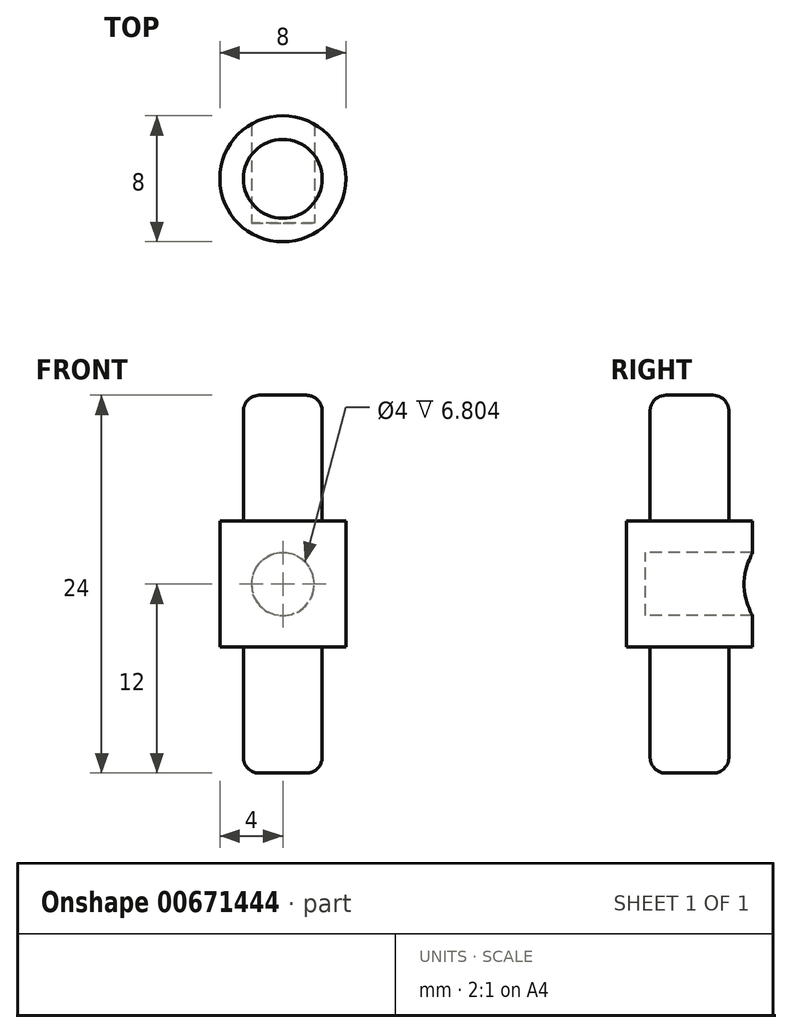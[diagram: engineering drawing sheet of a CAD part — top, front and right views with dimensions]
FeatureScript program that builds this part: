
annotation { "Feature Type Name" : "Feature", "Feature Type Description" : "" }
export const myFeature = defineFeature(function(context is Context, id is Id, definition is map)
    precondition{}
    {
        {
            var Q0;
            Q0=qCreatedBy(makeId("Top.planeOp"),FACE);
            var sketch = newSketch(context, id + "F0", { "sketchPlane" : qUnion([Q0])});
            skCircle(sketch, "E0", {"center": v(0, 0) * mm, "radius": 2.5 * mm});
            skCircle(sketch, "E1", {"center": v(0, 0) * mm, "radius": 4 * mm});
            skSolve(sketch);
        }
        {
            var Q0;
            Q0=makeQuery(id+"F0.imprint","IMPRINT",FACE,{"disambiguationData":[TD([[makeQuery(id+"F0.imprint","IMPRINT",EDGE,{"derivedFrom":sQuery(id+"F0.wireOp",EDGE,"E0")}),1.0]])]});
            extrude(context, id + "F1", {"entities" : qUnion([Q0]), "depth" : 12 * mm, "offsetDistance" : 25 * mm});
        }
        {
            var Q0;
            Q0=makeQuery(id+"F0.imprint","IMPRINT",FACE,{"disambiguationData":[TD([[makeQuery(id+"F0.imprint","IMPRINT",EDGE,{"derivedFrom":sQuery(id+"F0.wireOp",EDGE,"E0")}),1.0]])]});
            extrude(context, id + "F2", {"entities" : qUnion([Q0]), "operationType" : NewBodyOperationType.ADD, "oppositeDirection" : true, "depth" : 12 * mm, "offsetDistance" : 25 * mm});
        }
        {
            var Q0;
            Q0=makeQuery(id+"F0.imprint","IMPRINT",FACE,{"disambiguationData":[TD([[makeQuery(id+"F0.imprint","IMPRINT",EDGE,{"derivedFrom":sQuery(id+"F0.wireOp",EDGE,"E0")}),-1.0]])]});
            extrude(context, id + "F3", {"entities" : qUnion([Q0]), "operationType" : NewBodyOperationType.ADD, "depth" : 4 * mm, "offsetDistance" : 25 * mm});
        }
        {
            var Q0;
            Q0=makeQuery(id+"F0.imprint","IMPRINT",FACE,{"disambiguationData":[TD([[makeQuery(id+"F0.imprint","IMPRINT",EDGE,{"derivedFrom":sQuery(id+"F0.wireOp",EDGE,"E0")}),-1.0]])]});
            extrude(context, id + "F4", {"entities" : qUnion([Q0]), "operationType" : NewBodyOperationType.ADD, "oppositeDirection" : true, "depth" : 4 * mm, "offsetDistance" : 25 * mm});
        }
        {
            var Q0;
            Q0=makeQuery(id+"F1.opExtrude","CAP_EDGE",EDGE,{"disambiguationData":[OSD([sQuery(id+"F0.wireOp",EDGE,"E0")])],"isStart":false});
            var Q1;
            Q1=makeQuery(id+"F2.opExtrude","CAP_EDGE",EDGE,{"disambiguationData":[OSD([sQuery(id+"F0.wireOp",EDGE,"E0")])],"isStart":false});
            fillet(context, id + "F5", {"entities" : qUnion([Q0, Q1]), "radius" : 1 * mm, "tangentPropagation" : true, "allowEdgeOverflow" : false});
        }
        {
            var Q0;
            Q0=qCreatedBy(makeId("Front.planeOp"),FACE);
            var sketch = newSketch(context, id + "F6", { "sketchPlane" : qUnion([Q0])});
            skCircle(sketch, "E2", {"center": v(0, 0) * mm, "radius": 2 * mm});
            skSolve(sketch);
        }
        {
            var Q0;
            Q0=makeQuery(id+"F6.imprint","IMPRINT",FACE,{"disambiguationData":[TD([[makeQuery(id+"F6.imprint","IMPRINT",EDGE,{"derivedFrom":sQuery(id+"F6.wireOp",EDGE,"E2")}),1.0]])]});
            extrude(context, id + "F7", {"entities" : qUnion([Q0]), "operationType" : NewBodyOperationType.REMOVE, "oppositeDirection" : true, "depth" : 4.2 * mm, "offsetDistance" : 25 * mm});
        }
        {
            var Q0;
            Q0=makeQuery(id+"F6.imprint","IMPRINT",FACE,{"disambiguationData":[TD([[makeQuery(id+"F6.imprint","IMPRINT",EDGE,{"derivedFrom":sQuery(id+"F6.wireOp",EDGE,"E2")}),1.0]])]});
            extrude(context, id + "F8", {"entities" : qUnion([Q0]), "operationType" : NewBodyOperationType.REMOVE, "depth" : 2.8 * mm, "offsetDistance" : 25 * mm});
        }
    });
